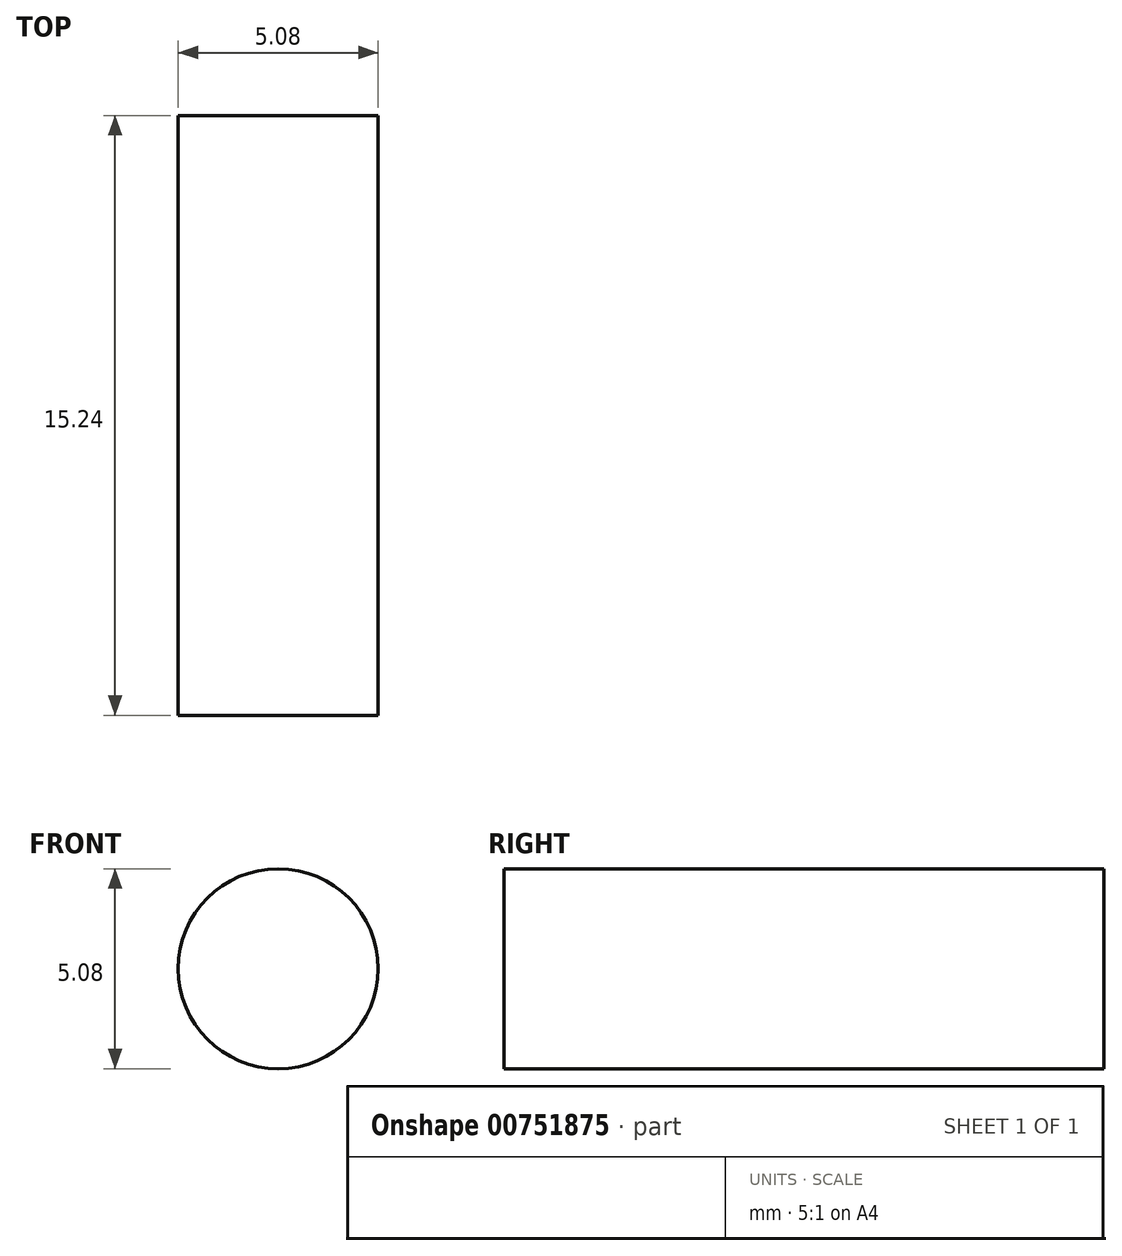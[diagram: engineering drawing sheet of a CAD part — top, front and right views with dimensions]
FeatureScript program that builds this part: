
annotation { "Feature Type Name" : "Feature", "Feature Type Description" : "" }
export const myFeature = defineFeature(function(context is Context, id is Id, definition is map)
    precondition{}
    {
        {
            var Q0;
            Q0=qCreatedBy(makeId("Front.planeOp"),FACE);
            var sketch = newSketch(context, id + "F0", { "sketchPlane" : qUnion([Q0])});
            skCircle(sketch, "E0", {"center": v(0, 0) * mm, "radius": 2.54 * mm});
            skSolve(sketch);
        }
        {
            var Q0;
            Q0=makeQuery(id+"F0.imprint","IMPRINT",FACE,{"disambiguationData":[TD([[makeQuery(id+"F0.imprint","IMPRINT",EDGE,{"derivedFrom":sQuery(id+"F0.wireOp",EDGE,"E0")}),1.0]])]});
            extrude(context, id + "F1", {"entities" : qUnion([Q0]), "depth" : 15.24 * mm, "offsetDistance" : 25.4 * mm});
        }
    });
